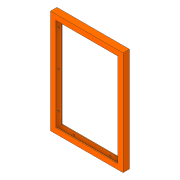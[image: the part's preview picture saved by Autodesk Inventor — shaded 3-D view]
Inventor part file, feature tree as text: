
AUTODESK INVENTOR PART (.ipt)
format: ipt  version: 2017 (Build 210142000, 142)  size: 135,680 bytes
history: native  units: mm
features: mirror x3, hole x2, extrude x1, shell x1, pattern_linear x1, sketch x1
ambient origin geometry x8: Origin, YZ Plane, XZ Plane, XY Plane, X Axis, Y Axis, Z Axis, Center Point
bodies: Solid1 (feature_tree)
feature tree (9):
  extrude  "Extrusion1"  Depth=177.8mm
  shell  "Shell1"  Thickness=13.0mm
  hole  "Hole1"  [1 undecoded]
  pattern_linear  "Rectangular Pattern1"  Spacing1=2.3622mm  [1 undecoded]
  mirror  "Mirror1"
  hole  "Hole2"  [1 undecoded]
  mirror  "Mirror2"
  mirror  "Mirror3"
  sketch  "Sketch1"  dims[d1=254.0mm d2=177.8mm d3=13.0mm d4=15.875mm d5=0.0mm d6=2.3622mm d8=6.35mm d9=127.0mm d10=4.496mm d11=6.35mm d12=8.433mm d13=2.0mm d14=14.3117mm d15=9.525mm d16=20.594885mm d17=30.0mm d19=88.9mm d20=6.35mm d21=133.35mm d22=4.496mm d23=6.35mm d24=8.433mm d25=2.0mm d26=14.3117mm d27=9.525mm d28=20.594885mm]
note: 3 required parameter values undecoded (feature->parameter linkage not recoverable at this tier; creation-order binding heuristic only, values carry confidence <= 0.55)
